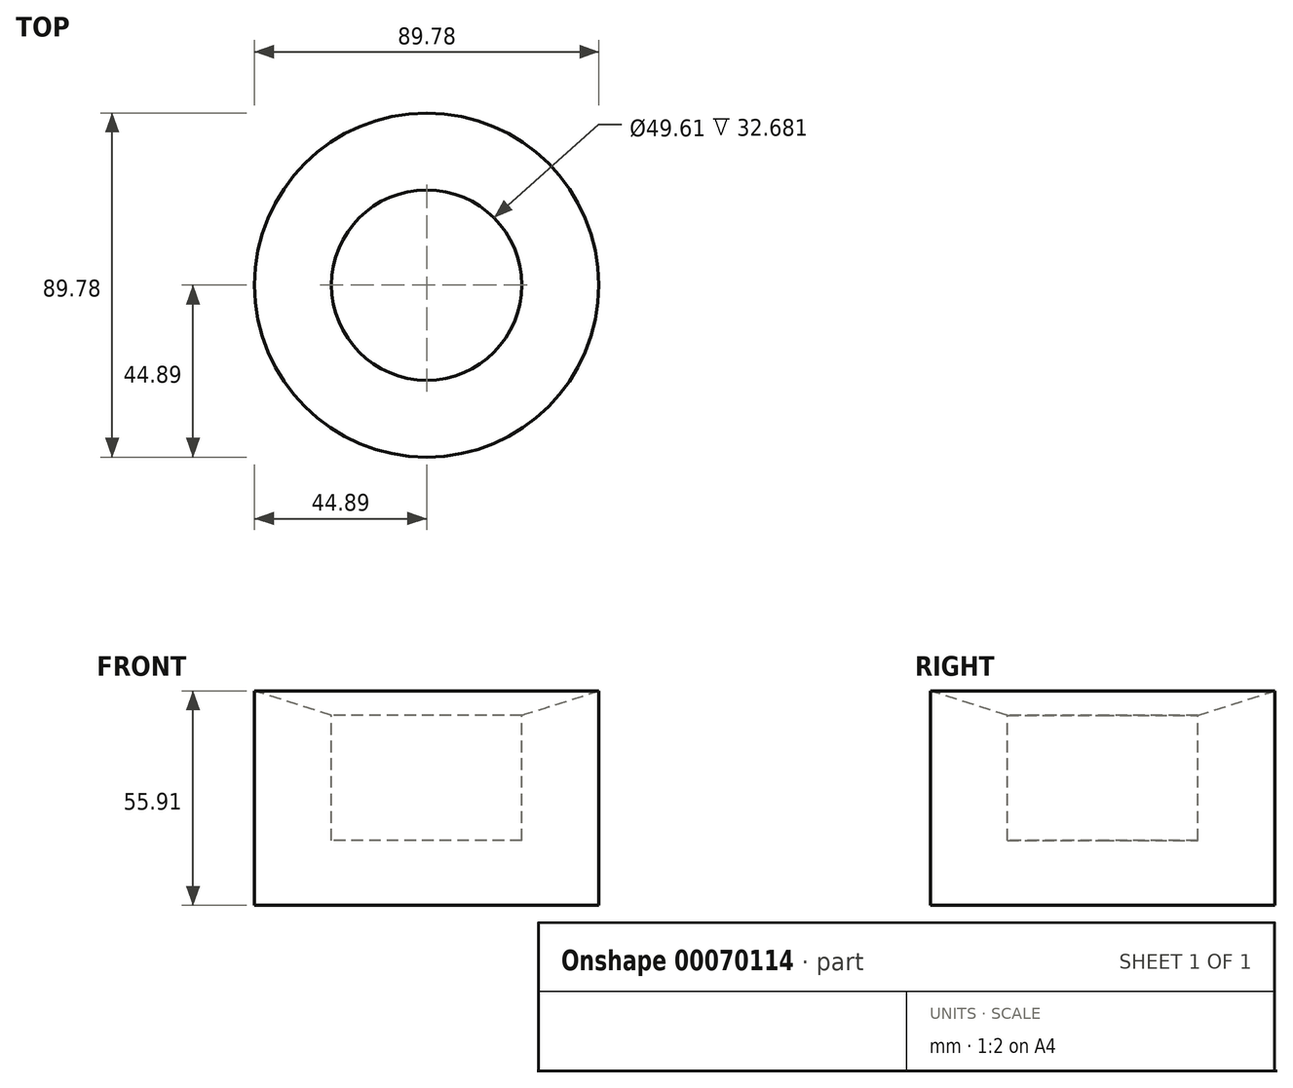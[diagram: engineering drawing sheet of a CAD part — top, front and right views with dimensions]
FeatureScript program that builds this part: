
annotation { "Feature Type Name" : "Feature", "Feature Type Description" : "" }
export const myFeature = defineFeature(function(context is Context, id is Id, definition is map)
    precondition{}
    {
        {
            var Q0;
            Q0=qCreatedBy(makeId("Front.planeOp"),FACE);
            var sketch = newSketch(context, id + "F0", { "sketchPlane" : qUnion([Q0])});
            skLineSegment(sketch, "E0", {"start": v(0, 0) * mm, "end": v(-44.89, 0) * mm});
            skLineSegment(sketch, "E1", {"start": v(-44.89, 0) * mm, "end": v(-44.89, 55.91) * mm});
            skLineSegment(sketch, "E2", {"start": v(-44.89, 55.91) * mm, "end": v(-24.8, 49.61) * mm});
            skLineSegment(sketch, "E3", {"start": v(-24.8, 49.61) * mm, "end": v(-24.8, 16.93) * mm});
            skLineSegment(sketch, "E4", {"start": v(-24.8, 16.93) * mm, "end": v(0, 16.93) * mm});
            skLineSegment(sketch, "E5", {"start": v(0, 16.93) * mm, "end": v(0, 0) * mm});
            skSolve(sketch);
        }
        {
            var Q0;
            Q0=makeQuery(id+"F0.imprint","IMPRINT",FACE,{"disambiguationData":[TD([[makeQuery(id+"F0.imprint","IMPRINT",EDGE,{"derivedFrom":sQuery(id+"F0.wireOp",EDGE,"E0")}),-1.0]])]});
            var Q1;
            Q1=sQuery(id+"F0.wireOp",EDGE,"E5");
            revolve(context, id + "F1", {"entities" : qUnion([Q0]), "axis" : qUnion([Q1]), "revolveType" : RevolveType.FULL});
        }
    });
